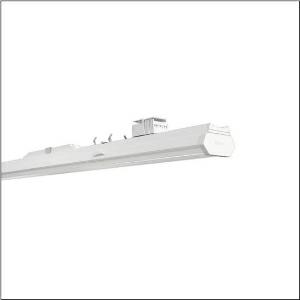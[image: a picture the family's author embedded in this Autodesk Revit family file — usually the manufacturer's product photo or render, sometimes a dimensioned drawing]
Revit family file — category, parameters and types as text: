
# Revit family: licross_r__11_protected_ho_51td12dn4fxm3c_9ee7
name_source: partatom
category: Lighting Fixtures
units: mm (PartAtom-declared; Revit-internal decimal feet)

## family parameters
Cut with Voids When Loaded = No
Host = Face
Light Source = No
Part Type = Normal
Room Calculation Point = No
Round Connector Dimension = Use Diameter
Shared = No

## types (1)
- --- (1 x LED, 970 lm, 7.4 W, 4000K)
    Apparent Load = 7 VA
    CIE Flux Codes = 70 91 97 98 100
    Color Rendering = 80
    Color Temperature = 4000K
    Default Elevation = 1800 mm
    Description = Licross® 11 Protected HO, luminaire insert, of sheet steel, galvanised, coil coated, white, length: 1.500mm, width: 90mm, height: 101mm, LED rated luminous flux: 15.270lm, light colour: 840, control gear: DALI 2 (for two DALI lines), with plug, 6-pole, with phase selection, for trunking rail, 14-core, mains connection: 220..240V, AC, 50/60Hz, rated input power: 91W, for trunking rail, 14-core, internal wiring halogen-free, for emergency light function, converter,control gear: single battery element, battery: LiFePO4, 9Ah, primary light control with lens, of plastic, primary optical cover: cover, of PMMA, light emission: direct distribution, primary light characteristic: symmetric, protection rating (complete): IP54, insulation class (complete): insulation class I (protective earthing), certification: CE, UKCA, protection symbol: D if used in an environment with non-conductive dust loads with corresponding accessories, impact resistance: IK06, permissible ambient temperature for indoor applications: +5..+30°C, standard: EN 60598-2-22, LABS conformity tested according to VDMA 24364:2018-05, reducing of maximum allowable ambient temperature of 5°C with ceiling mounting, corresponds to IFS (International Featured Standards) requirements for safety and quality in the food industry, packaging unit: 1 piece
    Height = 92 mm
    Lamp = 1 x LED
    Lamp Light Flux = 970 lm
    Lamp Power = 7.4 W
    Lamp count = 1
    Length = 1500 mm
    Luminous efficacy = 131 lm/W
    Manufacturer = Siteco
    ModVariant = No
    Model = 51TD12DN4FXM3C
    Mounting Place = Ceiling
    Mounting Type = Pendant
    Number of Poles = 1
    OnlyDefault = Yes
    Power Factor = 1
    Product Name = Licross® 11 Protected HO
    Product group = luminaire insert | ceiling pendant
    ProductGroupID = 902
    Protection Class = Protection class I
    Protection Degree = IP 54
    RLX_Detail_Level = 1
    RLX_Emergency_Light_Flux = 0 lm
    RLX_Emergency_Type = 0
    RLX_Emergency_Type_DB = No
    RlxData = <blob elided: 24897 chars, md5=cdd2b859>
    Socket = socket
    Standby Power = 0 W
    System Light Flux = 970 lm
    System Power = 7 W
    Type Comments = : emergency light operation: 3 h
    Type Image = l_1256145.jpg
    URL = http://relux.com
    VarID = @adj_112455
    Voltage = 0 V
    Weight = 0.00 kg
    Width = 88 mm

## geometry (parser evidence)
native form markers: Blend x4, Sweep x10
no freeform markers — native parametric forms only
